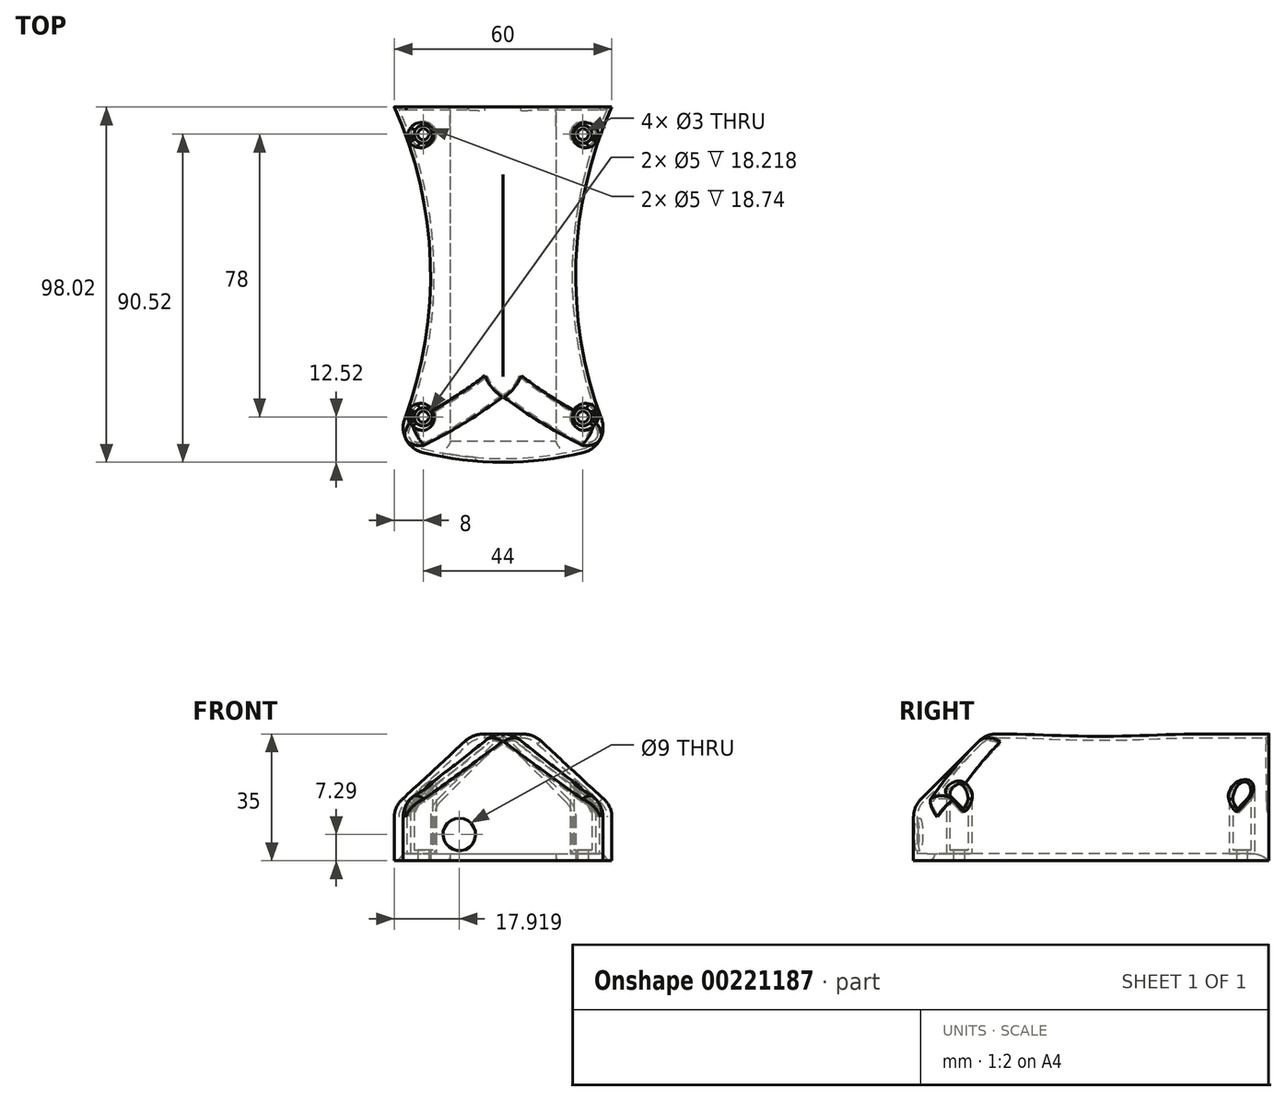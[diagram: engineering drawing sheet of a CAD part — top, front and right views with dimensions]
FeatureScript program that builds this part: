
annotation { "Feature Type Name" : "Feature", "Feature Type Description" : "" }
export const myFeature = defineFeature(function(context is Context, id is Id, definition is map)
    precondition{}
    {
        {
            var Q0;
            Q0=qCreatedBy(makeId("Top.planeOp"),FACE);
            var sketch = newSketch(context, id + "F0", { "sketchPlane" : qUnion([Q0])});
            skLineSegment(sketch, "E0.bottom", {"start": v(30, 46.5) * mm, "end": v(-30, 46.5) * mm});
            skPoint(sketch, "E0.middle", {"position": v(0, 0) * mm});
            skLineSegment(sketch, "E1.bottom", {"start": v(20.5, -39) * mm, "end": v(19.5, -39) * mm});
            skArc(sketch, "E2", {"start": v(30, 46.5) * mm, "mid": v(20.03, 2.3) * mm, "end": v(28.2, -42.26) * mm});
            skArc(sketch, "E3.MirrorCS", {"start": v(-30, 46.5) * mm, "mid": v(-20.03, 2.3) * mm, "end": v(-28.2, -42.26) * mm});
            skArc(sketch, "E4", {"start": v(-25.43, -47.94) * mm, "mid": v(0, -51.52) * mm, "end": v(25.43, -47.94) * mm});
            skCircle(sketch, "E5", {"center": v(-22, 39) * mm, "radius": 1.5 * mm});
            skCircle(sketch, "E6", {"center": v(22, 39) * mm, "radius": 1.5 * mm});
            skCircle(sketch, "E7", {"center": v(22, -39) * mm, "radius": 1.5 * mm});
            skCircle(sketch, "E8", {"center": v(-22, -39) * mm, "radius": 1.5 * mm});
            skLineSegment(sketch, "E9", {"start": v(28.2, -42.26) * mm, "end": v(25.43, -47.94) * mm});
            skLineSegment(sketch, "E10.MirrorCS", {"start": v(-28.2, -42.26) * mm, "end": v(-25.43, -47.94) * mm});
            skPoint(sketch, "E11.orphan", {"position": v(30, -46.5) * mm});
            skPoint(sketch, "E12.orphan", {"position": v(-30, -46.5) * mm});
            skCircle(sketch, "E13", {"center": v(-22, 39) * mm, "radius": 2.5 * mm});
            skCircle(sketch, "E14", {"center": v(22, 39) * mm, "radius": 2.5 * mm});
            skCircle(sketch, "E15", {"center": v(-22, -39) * mm, "radius": 2.5 * mm});
            skCircle(sketch, "E16", {"center": v(22, -39) * mm, "radius": 2.5 * mm});
            skLineSegment(sketch, "E17.bottom", {"start": v(16.76, 44.51) * mm, "end": v(-16.76, 44.51) * mm});
            skLineSegment(sketch, "E17.top", {"start": v(16.76, -44.51) * mm, "end": v(-16.76, -44.51) * mm});
            skLineSegment(sketch, "E17.left", {"start": v(16.76, 44.51) * mm, "end": v(16.76, -44.51) * mm});
            skLineSegment(sketch, "E17.right", {"start": v(-16.76, 44.51) * mm, "end": v(-16.76, -44.51) * mm});
            skSolve(sketch);
        }
        {
            var Q0;
            Q0=makeQuery(id+"F0.imprint","IMPRINT",FACE,{"disambiguationData":[TD([[makeQuery(id+"F0.imprint","IMPRINT",EDGE,{"derivedFrom":sQuery(id+"F0.wireOp",EDGE,"E0.bottom")}),1.0]])]});
            var Q1;
            Q1=makeQuery(id+"F0.imprint","IMPRINT",FACE,{"disambiguationData":[TD([[makeQuery(id+"F0.imprint","IMPRINT",EDGE,{"derivedFrom":sQuery(id+"F0.wireOp",EDGE,"E13")}),1.0]])]});
            var Q2;
            Q2=makeQuery(id+"F0.imprint","IMPRINT",FACE,{"disambiguationData":[TD([[makeQuery(id+"F0.imprint","IMPRINT",EDGE,{"derivedFrom":sQuery(id+"F0.wireOp",EDGE,"E14")}),1.0]])]});
            var Q3;
            Q3=makeQuery(id+"F0.imprint","IMPRINT",FACE,{"disambiguationData":[TD([[makeQuery(id+"F0.imprint","IMPRINT",EDGE,{"derivedFrom":sQuery(id+"F0.wireOp",EDGE,"E16")}),1.0]])]});
            var Q4;
            Q4=makeQuery(id+"F0.imprint","IMPRINT",FACE,{"disambiguationData":[TD([[makeQuery(id+"F0.imprint","IMPRINT",EDGE,{"derivedFrom":sQuery(id+"F0.wireOp",EDGE,"E15")}),1.0]])]});
            var Q5;
            Q5=makeQuery(id+"F0.imprint","IMPRINT",FACE,{"disambiguationData":[TD([[makeQuery(id+"F0.imprint","IMPRINT",EDGE,{"derivedFrom":sQuery(id+"F0.wireOp",EDGE,"SKrwtrik-Ue9O-fv6v-n90H-pNgHu3pozgwR")}),-1.0]])]});
            extrude(context, id + "F1", {"entities" : qUnion([Q0, Q1, Q2, Q3, Q4, Q5]), "depth" : 3 * mm});
        }
        {
            var Q0;
            Q0=makeQuery(id+"F0.imprint","IMPRINT",FACE,{"disambiguationData":[TD([[makeQuery(id+"F0.imprint","IMPRINT",EDGE,{"derivedFrom":sQuery(id+"F0.wireOp",EDGE,"E0.bottom")}),1.0]])]});
            var Q1;
            Q1=makeQuery(id+"F0.imprint","IMPRINT",FACE,{"disambiguationData":[TD([[makeQuery(id+"F0.imprint","IMPRINT",EDGE,{"derivedFrom":sQuery(id+"F0.wireOp",EDGE,"E17.bottom")}),1.0]])]});
            extrude(context, id + "F2", {"entities" : qUnion([Q0, Q1]), "operationType" : NewBodyOperationType.ADD, "depth" : 35 * mm});
        }
        {
            var Q0;
            Q0=makeQuery(id+"F2.opExtrude","CAP_EDGE",EDGE,{"disambiguationData":[OSD([sQuery(id+"F0.wireOp",EDGE,"E3.MirrorCS")])],"isStart":false});
            var Q1;
            Q1=makeQuery(id+"F2.opExtrude","CAP_EDGE",EDGE,{"disambiguationData":[OSD([sQuery(id+"F0.wireOp",EDGE,"E2")])],"isStart":false});
            var Q2;
            Q2=makeQuery(id+"F2.opExtrude","CAP_EDGE",EDGE,{"disambiguationData":[OSD([sQuery(id+"F0.wireOp",EDGE,"E4")])],"isStart":false});
            chamfer(context, id + "F3", {"entities" : qUnion([Q0, Q1, Q2]), "width" : 20 * mm, "tangentPropagation" : true});
        }
        {
            var Q0;
            {var subQ0=sQuery(id+"F0.wireOp",EDGE,"E3.MirrorCS");Q0=makeQuery(id+"F3.opChamfer","BLEND_EDGE",EDGE,{"blendedFrom":[makeQuery(id+"F2.opExtrude","CAP_EDGE",EDGE,{"disambiguationData":[OSD([subQ0])],"isStart":false}),makeQuery(id+"F2.boolean.opBoolean","MERGE",FACE,{"derivedFrom":[makeQuery(id+"F1.opExtrude","SWEPT_FACE",FACE,{"disambiguationData":[OSD([subQ0])]}),makeQuery(id+"F2.opExtrude","SWEPT_FACE",FACE,{"disambiguationData":[OSD([subQ0])]})]})],"blendedInto":[makeQuery(id+"F2.boolean.opBoolean","MERGE",FACE,{"derivedFrom":[makeQuery(id+"F1.opExtrude","SWEPT_FACE",FACE,{"disambiguationData":[OSD([subQ0])]}),makeQuery(id+"F2.opExtrude","SWEPT_FACE",FACE,{"disambiguationData":[OSD([subQ0])]})]})]});}
            var Q1;
            {var subQ0=sQuery(id+"F0.wireOp",EDGE,"E2");Q1=makeQuery(id+"F3.opChamfer","BLEND_EDGE",EDGE,{"blendedFrom":[makeQuery(id+"F2.opExtrude","CAP_EDGE",EDGE,{"disambiguationData":[OSD([subQ0])],"isStart":false}),makeQuery(id+"F2.opExtrude","CAP_FACE",FACE,{"disambiguationData":[OSD([sQuery(id+"F0.wireOp",EDGE,"E0.bottom"),subQ0,sQuery(id+"F0.wireOp",EDGE,"E3.MirrorCS"),sQuery(id+"F0.wireOp",EDGE,"E4"),sQuery(id+"F0.wireOp",EDGE,"E9"),sQuery(id+"F0.wireOp",EDGE,"E10.MirrorCS"),sQuery(id+"F0.wireOp",EDGE,"SKrwtrik-Ue9O-fv6v-n90H-pNgHu3pozgwR"),sQuery(id+"F0.wireOp",EDGE,"E13"),sQuery(id+"F0.wireOp",EDGE,"E14"),sQuery(id+"F0.wireOp",EDGE,"E15"),sQuery(id+"F0.wireOp",EDGE,"E16")])],"isStart":false})],"blendedInto":[makeQuery(id+"F2.opExtrude","CAP_FACE",FACE,{"disambiguationData":[OSD([sQuery(id+"F0.wireOp",EDGE,"E0.bottom"),subQ0,sQuery(id+"F0.wireOp",EDGE,"E3.MirrorCS"),sQuery(id+"F0.wireOp",EDGE,"E4"),sQuery(id+"F0.wireOp",EDGE,"E9"),sQuery(id+"F0.wireOp",EDGE,"E10.MirrorCS"),sQuery(id+"F0.wireOp",EDGE,"SKrwtrik-Ue9O-fv6v-n90H-pNgHu3pozgwR"),sQuery(id+"F0.wireOp",EDGE,"E13"),sQuery(id+"F0.wireOp",EDGE,"E14"),sQuery(id+"F0.wireOp",EDGE,"E15"),sQuery(id+"F0.wireOp",EDGE,"E16")])],"isStart":false})]});}
            var Q2;
            {var subQ0=sQuery(id+"F0.wireOp",EDGE,"E3.MirrorCS");Q2=makeQuery(id+"F3.opChamfer","BLEND_EDGE",EDGE,{"blendedFrom":[makeQuery(id+"F2.opExtrude","CAP_EDGE",EDGE,{"disambiguationData":[OSD([subQ0])],"isStart":false}),makeQuery(id+"F2.opExtrude","CAP_FACE",FACE,{"disambiguationData":[OSD([sQuery(id+"F0.wireOp",EDGE,"E0.bottom"),sQuery(id+"F0.wireOp",EDGE,"E2"),subQ0,sQuery(id+"F0.wireOp",EDGE,"E4"),sQuery(id+"F0.wireOp",EDGE,"E9"),sQuery(id+"F0.wireOp",EDGE,"E10.MirrorCS"),sQuery(id+"F0.wireOp",EDGE,"SKrwtrik-Ue9O-fv6v-n90H-pNgHu3pozgwR"),sQuery(id+"F0.wireOp",EDGE,"E13"),sQuery(id+"F0.wireOp",EDGE,"E14"),sQuery(id+"F0.wireOp",EDGE,"E15"),sQuery(id+"F0.wireOp",EDGE,"E16")])],"isStart":false})],"blendedInto":[makeQuery(id+"F2.opExtrude","CAP_FACE",FACE,{"disambiguationData":[OSD([sQuery(id+"F0.wireOp",EDGE,"E0.bottom"),sQuery(id+"F0.wireOp",EDGE,"E2"),subQ0,sQuery(id+"F0.wireOp",EDGE,"E4"),sQuery(id+"F0.wireOp",EDGE,"E9"),sQuery(id+"F0.wireOp",EDGE,"E10.MirrorCS"),sQuery(id+"F0.wireOp",EDGE,"SKrwtrik-Ue9O-fv6v-n90H-pNgHu3pozgwR"),sQuery(id+"F0.wireOp",EDGE,"E13"),sQuery(id+"F0.wireOp",EDGE,"E14"),sQuery(id+"F0.wireOp",EDGE,"E15"),sQuery(id+"F0.wireOp",EDGE,"E16")])],"isStart":false})]});}
            var Q3;
            {var subQ0=sQuery(id+"F0.wireOp",EDGE,"E2");Q3=makeQuery(id+"F3.opChamfer","BLEND_EDGE",EDGE,{"blendedFrom":[makeQuery(id+"F2.opExtrude","CAP_EDGE",EDGE,{"disambiguationData":[OSD([subQ0])],"isStart":false}),makeQuery(id+"F2.boolean.opBoolean","MERGE",FACE,{"derivedFrom":[makeQuery(id+"F1.opExtrude","SWEPT_FACE",FACE,{"disambiguationData":[OSD([subQ0])]}),makeQuery(id+"F2.opExtrude","SWEPT_FACE",FACE,{"disambiguationData":[OSD([subQ0])]})]})],"blendedInto":[makeQuery(id+"F2.boolean.opBoolean","MERGE",FACE,{"derivedFrom":[makeQuery(id+"F1.opExtrude","SWEPT_FACE",FACE,{"disambiguationData":[OSD([subQ0])]}),makeQuery(id+"F2.opExtrude","SWEPT_FACE",FACE,{"disambiguationData":[OSD([subQ0])]})]})]});}
            var Q4;
            Q4=makeQuery(id+"F3.opChamfer","BLEND_EDGE",EDGE,{"blendedFrom":[makeQuery(id+"F2.opExtrude","CAP_EDGE",EDGE,{"disambiguationData":[OSD([sQuery(id+"F0.wireOp",EDGE,"E2")])],"isStart":false}),makeQuery(id+"F2.opExtrude","CAP_EDGE",EDGE,{"disambiguationData":[OSD([sQuery(id+"F0.wireOp",EDGE,"E4")])],"isStart":false})],"blendedInto":[]});
            var Q5;
            Q5=makeQuery(id+"F3.opChamfer","BLEND_EDGE",EDGE,{"blendedFrom":[makeQuery(id+"F2.opExtrude","CAP_EDGE",EDGE,{"disambiguationData":[OSD([sQuery(id+"F0.wireOp",EDGE,"E3.MirrorCS")])],"isStart":false}),makeQuery(id+"F2.opExtrude","CAP_EDGE",EDGE,{"disambiguationData":[OSD([sQuery(id+"F0.wireOp",EDGE,"E4")])],"isStart":false})],"blendedInto":[]});
            var Q6;
            {var subQ0=sQuery(id+"F0.wireOp",EDGE,"E4");Q6=makeQuery(id+"F3.opChamfer","BLEND_EDGE",EDGE,{"blendedFrom":[makeQuery(id+"F2.opExtrude","CAP_EDGE",EDGE,{"disambiguationData":[OSD([subQ0])],"isStart":false}),makeQuery(id+"F2.opExtrude","CAP_FACE",FACE,{"disambiguationData":[OSD([sQuery(id+"F0.wireOp",EDGE,"E0.bottom"),sQuery(id+"F0.wireOp",EDGE,"E2"),sQuery(id+"F0.wireOp",EDGE,"E3.MirrorCS"),subQ0,sQuery(id+"F0.wireOp",EDGE,"E9"),sQuery(id+"F0.wireOp",EDGE,"E10.MirrorCS"),sQuery(id+"F0.wireOp",EDGE,"SKrwtrik-Ue9O-fv6v-n90H-pNgHu3pozgwR"),sQuery(id+"F0.wireOp",EDGE,"E13"),sQuery(id+"F0.wireOp",EDGE,"E14"),sQuery(id+"F0.wireOp",EDGE,"E15"),sQuery(id+"F0.wireOp",EDGE,"E16")])],"isStart":false})],"blendedInto":[makeQuery(id+"F2.opExtrude","CAP_FACE",FACE,{"disambiguationData":[OSD([sQuery(id+"F0.wireOp",EDGE,"E0.bottom"),sQuery(id+"F0.wireOp",EDGE,"E2"),sQuery(id+"F0.wireOp",EDGE,"E3.MirrorCS"),subQ0,sQuery(id+"F0.wireOp",EDGE,"E9"),sQuery(id+"F0.wireOp",EDGE,"E10.MirrorCS"),sQuery(id+"F0.wireOp",EDGE,"SKrwtrik-Ue9O-fv6v-n90H-pNgHu3pozgwR"),sQuery(id+"F0.wireOp",EDGE,"E13"),sQuery(id+"F0.wireOp",EDGE,"E14"),sQuery(id+"F0.wireOp",EDGE,"E15"),sQuery(id+"F0.wireOp",EDGE,"E16")])],"isStart":false})]});}
            var Q7;
            {var subQ0=sQuery(id+"F0.wireOp",EDGE,"E4");Q7=makeQuery(id+"F3.opChamfer","BLEND_EDGE",EDGE,{"blendedFrom":[makeQuery(id+"F2.opExtrude","CAP_EDGE",EDGE,{"disambiguationData":[OSD([subQ0])],"isStart":false}),makeQuery(id+"F2.boolean.opBoolean","MERGE",FACE,{"derivedFrom":[makeQuery(id+"F1.opExtrude","SWEPT_FACE",FACE,{"disambiguationData":[OSD([subQ0])]}),makeQuery(id+"F2.opExtrude","SWEPT_FACE",FACE,{"disambiguationData":[OSD([subQ0])]})]})],"blendedInto":[makeQuery(id+"F2.boolean.opBoolean","MERGE",FACE,{"derivedFrom":[makeQuery(id+"F1.opExtrude","SWEPT_FACE",FACE,{"disambiguationData":[OSD([subQ0])]}),makeQuery(id+"F2.opExtrude","SWEPT_FACE",FACE,{"disambiguationData":[OSD([subQ0])]})]})]});}
            var Q8;
            {var subQ0=sQuery(id+"F0.wireOp",EDGE,"E9");Q8=makeQuery(id+"F3.opChamfer","BLEND_EDGE",EDGE,{"blendedFrom":[makeQuery(id+"F2.opExtrude","CAP_EDGE",EDGE,{"disambiguationData":[OSD([sQuery(id+"F0.wireOp",EDGE,"E2")])],"isStart":false}),makeQuery(id+"F2.boolean.opBoolean","MERGE",FACE,{"derivedFrom":[makeQuery(id+"F1.opExtrude","SWEPT_FACE",FACE,{"disambiguationData":[OSD([subQ0])]}),makeQuery(id+"F2.opExtrude","SWEPT_FACE",FACE,{"disambiguationData":[OSD([subQ0])]})]})],"blendedInto":[makeQuery(id+"F2.boolean.opBoolean","MERGE",FACE,{"derivedFrom":[makeQuery(id+"F1.opExtrude","SWEPT_FACE",FACE,{"disambiguationData":[OSD([subQ0])]}),makeQuery(id+"F2.opExtrude","SWEPT_FACE",FACE,{"disambiguationData":[OSD([subQ0])]})]})]});}
            var Q9;
            {var subQ0=sQuery(id+"F0.wireOp",EDGE,"E9");Q9=makeQuery(id+"F3.opChamfer","BLEND_EDGE",EDGE,{"blendedFrom":[makeQuery(id+"F2.opExtrude","CAP_EDGE",EDGE,{"disambiguationData":[OSD([sQuery(id+"F0.wireOp",EDGE,"E4")])],"isStart":false}),makeQuery(id+"F2.boolean.opBoolean","MERGE",FACE,{"derivedFrom":[makeQuery(id+"F1.opExtrude","SWEPT_FACE",FACE,{"disambiguationData":[OSD([subQ0])]}),makeQuery(id+"F2.opExtrude","SWEPT_FACE",FACE,{"disambiguationData":[OSD([subQ0])]})]})],"blendedInto":[makeQuery(id+"F2.boolean.opBoolean","MERGE",FACE,{"derivedFrom":[makeQuery(id+"F1.opExtrude","SWEPT_FACE",FACE,{"disambiguationData":[OSD([subQ0])]}),makeQuery(id+"F2.opExtrude","SWEPT_FACE",FACE,{"disambiguationData":[OSD([subQ0])]})]})]});}
            var Q10;
            {var subQ0=sQuery(id+"F0.wireOp",EDGE,"E9");var subQ1=sQuery(id+"F0.wireOp",EDGE,"E4");Q10=makeQuery(id+"F2.boolean.opBoolean","MERGE",EDGE,{"derivedFrom":[makeQuery(id+"F1.opExtrude","SWEPT_EDGE",EDGE,{"disambiguationData":[OSD([subQ1,subQ0])]}),makeQuery(id+"F2.opExtrude","SWEPT_EDGE",EDGE,{"disambiguationData":[OSD([subQ1,subQ0])]})]});}
            var Q11;
            {var subQ0=sQuery(id+"F0.wireOp",EDGE,"E9");var subQ1=sQuery(id+"F0.wireOp",EDGE,"E2");Q11=makeQuery(id+"F2.boolean.opBoolean","MERGE",EDGE,{"derivedFrom":[makeQuery(id+"F1.opExtrude","SWEPT_EDGE",EDGE,{"disambiguationData":[OSD([subQ1,subQ0])]}),makeQuery(id+"F2.opExtrude","SWEPT_EDGE",EDGE,{"disambiguationData":[OSD([subQ1,subQ0])]})]});}
            var Q12;
            {var subQ0=sQuery(id+"F0.wireOp",EDGE,"E10.MirrorCS");Q12=makeQuery(id+"F3.opChamfer","BLEND_EDGE",EDGE,{"blendedFrom":[makeQuery(id+"F2.opExtrude","CAP_EDGE",EDGE,{"disambiguationData":[OSD([sQuery(id+"F0.wireOp",EDGE,"E4")])],"isStart":false}),makeQuery(id+"F2.boolean.opBoolean","MERGE",FACE,{"derivedFrom":[makeQuery(id+"F1.opExtrude","SWEPT_FACE",FACE,{"disambiguationData":[OSD([subQ0])]}),makeQuery(id+"F2.opExtrude","SWEPT_FACE",FACE,{"disambiguationData":[OSD([subQ0])]})]})],"blendedInto":[makeQuery(id+"F2.boolean.opBoolean","MERGE",FACE,{"derivedFrom":[makeQuery(id+"F1.opExtrude","SWEPT_FACE",FACE,{"disambiguationData":[OSD([subQ0])]}),makeQuery(id+"F2.opExtrude","SWEPT_FACE",FACE,{"disambiguationData":[OSD([subQ0])]})]})]});}
            var Q13;
            {var subQ0=sQuery(id+"F0.wireOp",EDGE,"E10.MirrorCS");Q13=makeQuery(id+"F3.opChamfer","BLEND_EDGE",EDGE,{"blendedFrom":[makeQuery(id+"F2.opExtrude","CAP_EDGE",EDGE,{"disambiguationData":[OSD([sQuery(id+"F0.wireOp",EDGE,"E3.MirrorCS")])],"isStart":false}),makeQuery(id+"F2.boolean.opBoolean","MERGE",FACE,{"derivedFrom":[makeQuery(id+"F1.opExtrude","SWEPT_FACE",FACE,{"disambiguationData":[OSD([subQ0])]}),makeQuery(id+"F2.opExtrude","SWEPT_FACE",FACE,{"disambiguationData":[OSD([subQ0])]})]})],"blendedInto":[makeQuery(id+"F2.boolean.opBoolean","MERGE",FACE,{"derivedFrom":[makeQuery(id+"F1.opExtrude","SWEPT_FACE",FACE,{"disambiguationData":[OSD([subQ0])]}),makeQuery(id+"F2.opExtrude","SWEPT_FACE",FACE,{"disambiguationData":[OSD([subQ0])]})]})]});}
            var Q14;
            {var subQ0=sQuery(id+"F0.wireOp",EDGE,"E10.MirrorCS");var subQ1=sQuery(id+"F0.wireOp",EDGE,"E3.MirrorCS");Q14=makeQuery(id+"F2.boolean.opBoolean","MERGE",EDGE,{"derivedFrom":[makeQuery(id+"F1.opExtrude","SWEPT_EDGE",EDGE,{"disambiguationData":[OSD([subQ1,subQ0])]}),makeQuery(id+"F2.opExtrude","SWEPT_EDGE",EDGE,{"disambiguationData":[OSD([subQ1,subQ0])]})]});}
            var Q15;
            {var subQ0=sQuery(id+"F0.wireOp",EDGE,"E10.MirrorCS");var subQ1=sQuery(id+"F0.wireOp",EDGE,"E4");Q15=makeQuery(id+"F2.boolean.opBoolean","MERGE",EDGE,{"derivedFrom":[makeQuery(id+"F1.opExtrude","SWEPT_EDGE",EDGE,{"disambiguationData":[OSD([subQ1,subQ0])]}),makeQuery(id+"F2.opExtrude","SWEPT_EDGE",EDGE,{"disambiguationData":[OSD([subQ1,subQ0])]})]});}
            fillet(context, id + "F4", {"entities" : qUnion([Q0, Q1, Q2, Q3, Q4, Q5, Q6, Q7, Q8, Q9, Q10, Q11, Q12, Q13, Q14, Q15]), "radius" : 7 * mm, "tangentPropagation" : true, "allowEdgeOverflow" : false});
        }
        {
            var Q0;
            Q0=makeQuery(id+"F3.opChamfer","BLEND_EDGE",EDGE,{"blendedFrom":[makeQuery(id+"F2.opExtrude","CAP_EDGE",EDGE,{"disambiguationData":[OSD([sQuery(id+"F0.wireOp",EDGE,"E2")])],"isStart":false}),makeQuery(id+"F2.opExtrude","SWEPT_FACE",FACE,{"disambiguationData":[OSD([sQuery(id+"F0.wireOp",EDGE,"E14")])]})],"blendedInto":[makeQuery(id+"F2.opExtrude","SWEPT_FACE",FACE,{"disambiguationData":[OSD([sQuery(id+"F0.wireOp",EDGE,"E14")])]})]});
            var Q1;
            Q1=makeQuery(id+"F3.opChamfer","BLEND_EDGE",EDGE,{"blendedFrom":[makeQuery(id+"F2.opExtrude","CAP_EDGE",EDGE,{"disambiguationData":[OSD([sQuery(id+"F0.wireOp",EDGE,"E3.MirrorCS")])],"isStart":false}),makeQuery(id+"F2.opExtrude","SWEPT_FACE",FACE,{"disambiguationData":[OSD([sQuery(id+"F0.wireOp",EDGE,"E13")])]})],"blendedInto":[makeQuery(id+"F2.opExtrude","SWEPT_FACE",FACE,{"disambiguationData":[OSD([sQuery(id+"F0.wireOp",EDGE,"E13")])]})]});
            var Q2;
            Q2=makeQuery(id+"F3.opChamfer","BLEND_EDGE",EDGE,{"blendedFrom":[makeQuery(id+"F2.opExtrude","CAP_EDGE",EDGE,{"disambiguationData":[OSD([sQuery(id+"F0.wireOp",EDGE,"E3.MirrorCS")])],"isStart":false}),makeQuery(id+"F2.opExtrude","SWEPT_FACE",FACE,{"disambiguationData":[OSD([sQuery(id+"F0.wireOp",EDGE,"E15")])]})],"blendedInto":[makeQuery(id+"F2.opExtrude","SWEPT_FACE",FACE,{"disambiguationData":[OSD([sQuery(id+"F0.wireOp",EDGE,"E15")])]})]});
            var Q3;
            Q3=makeQuery(id+"F4.opFillet","BLEND_EDGE",EDGE,{"blendedFrom":[makeQuery(id+"F3.opChamfer","BLEND_EDGE",EDGE,{"blendedFrom":[makeQuery(id+"F2.opExtrude","CAP_EDGE",EDGE,{"disambiguationData":[OSD([sQuery(id+"F0.wireOp",EDGE,"E3.MirrorCS")])],"isStart":false}),makeQuery(id+"F2.opExtrude","CAP_EDGE",EDGE,{"disambiguationData":[OSD([sQuery(id+"F0.wireOp",EDGE,"E4")])],"isStart":false})],"blendedInto":[]}),makeQuery(id+"F2.opExtrude","SWEPT_FACE",FACE,{"disambiguationData":[OSD([sQuery(id+"F0.wireOp",EDGE,"E15")])]})],"blendedInto":[makeQuery(id+"F2.opExtrude","SWEPT_FACE",FACE,{"disambiguationData":[OSD([sQuery(id+"F0.wireOp",EDGE,"E15")])]})]});
            var Q4;
            Q4=makeQuery(id+"F3.opChamfer","BLEND_EDGE",EDGE,{"blendedFrom":[makeQuery(id+"F2.opExtrude","CAP_EDGE",EDGE,{"disambiguationData":[OSD([sQuery(id+"F0.wireOp",EDGE,"E2")])],"isStart":false}),makeQuery(id+"F2.opExtrude","SWEPT_FACE",FACE,{"disambiguationData":[OSD([sQuery(id+"F0.wireOp",EDGE,"E16")])]})],"blendedInto":[makeQuery(id+"F2.opExtrude","SWEPT_FACE",FACE,{"disambiguationData":[OSD([sQuery(id+"F0.wireOp",EDGE,"E16")])]})]});
            var Q5;
            Q5=makeQuery(id+"F4.opFillet","BLEND_EDGE",EDGE,{"blendedFrom":[makeQuery(id+"F3.opChamfer","BLEND_EDGE",EDGE,{"blendedFrom":[makeQuery(id+"F2.opExtrude","CAP_EDGE",EDGE,{"disambiguationData":[OSD([sQuery(id+"F0.wireOp",EDGE,"E2")])],"isStart":false}),makeQuery(id+"F2.opExtrude","CAP_EDGE",EDGE,{"disambiguationData":[OSD([sQuery(id+"F0.wireOp",EDGE,"E4")])],"isStart":false})],"blendedInto":[]}),makeQuery(id+"F2.opExtrude","SWEPT_FACE",FACE,{"disambiguationData":[OSD([sQuery(id+"F0.wireOp",EDGE,"E16")])]})],"blendedInto":[makeQuery(id+"F2.opExtrude","SWEPT_FACE",FACE,{"disambiguationData":[OSD([sQuery(id+"F0.wireOp",EDGE,"E16")])]})]});
            fillet(context, id + "F5", {"entities" : qUnion([Q0, Q1, Q2, Q3, Q4, Q5]), "radius" : 1 * mm, "tangentPropagation" : true, "allowEdgeOverflow" : false});
        }
        {
            var Q0;
            {var subQ0=sQuery(id+"F0.wireOp",EDGE,"E0.bottom");Q0=makeQuery(id+"F2.boolean.opBoolean","MERGE",FACE,{"derivedFrom":[makeQuery(id+"F1.opExtrude","SWEPT_FACE",FACE,{"disambiguationData":[OSD([subQ0])]}),makeQuery(id+"F2.opExtrude","SWEPT_FACE",FACE,{"disambiguationData":[OSD([subQ0])]})]});}
            shell(context, id + "F6", {"entities" : qUnion([Q0]), "thickness" : 1 * mm});
        }
        {
            var Q0;
            Q0=makeQuery(id+"F6.opShell","OFFSET_FACE",FACE,{"disambiguationData":[OSD([sQuery(id+"F0.wireOp",EDGE,"E0.bottom"),sQuery(id+"F0.wireOp",EDGE,"E2"),sQuery(id+"F0.wireOp",EDGE,"E3.MirrorCS"),sQuery(id+"F0.wireOp",EDGE,"E4"),sQuery(id+"F0.wireOp",EDGE,"E5"),sQuery(id+"F0.wireOp",EDGE,"E6"),sQuery(id+"F0.wireOp",EDGE,"E7"),sQuery(id+"F0.wireOp",EDGE,"E8"),sQuery(id+"F0.wireOp",EDGE,"E9"),sQuery(id+"F0.wireOp",EDGE,"E10.MirrorCS"),sQuery(id+"F0.wireOp",EDGE,"E13"),sQuery(id+"F0.wireOp",EDGE,"E14"),sQuery(id+"F0.wireOp",EDGE,"E15"),sQuery(id+"F0.wireOp",EDGE,"E16"),sQuery(id+"F0.wireOp",EDGE,"E17.bottom"),sQuery(id+"F0.wireOp",EDGE,"E17.top"),sQuery(id+"F0.wireOp",EDGE,"E17.left"),sQuery(id+"F0.wireOp",EDGE,"E17.right")])]});
            extrude(context, id + "F7", {"entities" : qUnion([Q0]), "operationType" : NewBodyOperationType.ADD, "depth" : 1 * mm});
        }
        {
            var Q0;
            Q0=makeQuery(id+"F7.opExtrude","CAP_FACE",FACE,{"disambiguationData":[OSD([sQuery(id+"F0.wireOp",EDGE,"E0.bottom"),sQuery(id+"F0.wireOp",EDGE,"E2"),sQuery(id+"F0.wireOp",EDGE,"E3.MirrorCS"),sQuery(id+"F0.wireOp",EDGE,"E4"),sQuery(id+"F0.wireOp",EDGE,"E5"),sQuery(id+"F0.wireOp",EDGE,"E6"),sQuery(id+"F0.wireOp",EDGE,"E7"),sQuery(id+"F0.wireOp",EDGE,"E8"),sQuery(id+"F0.wireOp",EDGE,"E9"),sQuery(id+"F0.wireOp",EDGE,"E10.MirrorCS"),sQuery(id+"F0.wireOp",EDGE,"E13"),sQuery(id+"F0.wireOp",EDGE,"E14"),sQuery(id+"F0.wireOp",EDGE,"E15"),sQuery(id+"F0.wireOp",EDGE,"E16"),sQuery(id+"F0.wireOp",EDGE,"E17.bottom"),sQuery(id+"F0.wireOp",EDGE,"E17.top"),sQuery(id+"F0.wireOp",EDGE,"E17.left"),sQuery(id+"F0.wireOp",EDGE,"E17.right")])],"isStart":false});
            var sketch = newSketch(context, id + "F8", { "sketchPlane" : qUnion([Q0])});
            skLineSegment(sketch, "E18.bottom", {"start": v(-14.58, 54.73) * mm, "end": v(14.58, 54.73) * mm});
            skLineSegment(sketch, "E18.top", {"start": v(-14.58, -45.6) * mm, "end": v(14.58, -45.6) * mm});
            skLineSegment(sketch, "E18.left", {"start": v(-14.58, 54.73) * mm, "end": v(-14.58, -45.6) * mm});
            skLineSegment(sketch, "E18.right", {"start": v(14.58, 54.73) * mm, "end": v(14.58, -45.6) * mm});
            skPoint(sketch, "E18.middle", {"position": v(0, 4.56) * mm});
            skSolve(sketch);
        }
        {
            var Q0;
            {var subQ0=sQuery(id+"F8.wireOp",EDGE,"E18.top");Q0=makeQuery(id+"F8.imprint","IMPRINT",FACE,{"disambiguationData":[TD([[makeQuery(id+"F8.imprint","IMPRINT",EDGE,{"derivedFrom":subQ0}),1.0]])]});}
            extrude(context, id + "F9", {"entities" : qUnion([Q0]), "operationType" : NewBodyOperationType.REMOVE, "oppositeDirection" : true, "depth" : 3 * mm});
        }
        {
            var Q0;
            Q0=makeQuery(id+"F9.boolean.opBoolean","COPY",EDGE,{"derivedFrom":makeQuery(id+"F9.opExtrude","CAP_EDGE",EDGE,{"disambiguationData":[OSD([sQuery(id+"F8.wireOp",EDGE,"E18.right")])],"isStart":true})});
            var Q1;
            {var subQ0=sQuery(id+"F0.wireOp",EDGE,"E10.MirrorCS");var subQ1=sQuery(id+"F0.wireOp",EDGE,"E9");var subQ2=sQuery(id+"F0.wireOp",EDGE,"E4");var subQ3=sQuery(id+"F0.wireOp",EDGE,"E3.MirrorCS");var subQ4=sQuery(id+"F0.wireOp",EDGE,"E2");var subQ5=sQuery(id+"F0.wireOp",EDGE,"E0.bottom");Q1=makeQuery(id+"F9.boolean.opBoolean","INTERSECT",EDGE,{"derivedFrom":[makeQuery(id+"F2.boolean.opBoolean","MERGE",FACE,{"derivedFrom":[makeQuery(id+"F1.opExtrude","CAP_FACE",FACE,{"disambiguationData":[OSD([subQ5,subQ4,subQ3,subQ2,sQuery(id+"F0.wireOp",EDGE,"E5"),sQuery(id+"F0.wireOp",EDGE,"E6"),sQuery(id+"F0.wireOp",EDGE,"E7"),sQuery(id+"F0.wireOp",EDGE,"E8"),subQ1,subQ0,sQuery(id+"F0.wireOp",EDGE,"E17.bottom"),sQuery(id+"F0.wireOp",EDGE,"E17.top"),sQuery(id+"F0.wireOp",EDGE,"E17.left"),sQuery(id+"F0.wireOp",EDGE,"E17.right")])],"isStart":true}),makeQuery(id+"F2.opExtrude","CAP_FACE",FACE,{"disambiguationData":[OSD([subQ5,subQ4,subQ3,subQ2,subQ1,subQ0,sQuery(id+"F0.wireOp",EDGE,"E13"),sQuery(id+"F0.wireOp",EDGE,"E14"),sQuery(id+"F0.wireOp",EDGE,"E15"),sQuery(id+"F0.wireOp",EDGE,"E16")])],"isStart":true})]}),makeQuery(id+"F9.opExtrude","SWEPT_FACE",FACE,{"disambiguationData":[OSD([sQuery(id+"F8.wireOp",EDGE,"E18.right")])]})]});}
            var Q2;
            Q2=makeQuery(id+"F9.boolean.opBoolean","COPY",EDGE,{"derivedFrom":makeQuery(id+"F9.opExtrude","CAP_EDGE",EDGE,{"disambiguationData":[OSD([sQuery(id+"F8.wireOp",EDGE,"E18.left")])],"isStart":true})});
            var Q3;
            {var subQ0=sQuery(id+"F0.wireOp",EDGE,"E10.MirrorCS");var subQ1=sQuery(id+"F0.wireOp",EDGE,"E9");var subQ2=sQuery(id+"F0.wireOp",EDGE,"E4");var subQ3=sQuery(id+"F0.wireOp",EDGE,"E3.MirrorCS");var subQ4=sQuery(id+"F0.wireOp",EDGE,"E2");var subQ5=sQuery(id+"F0.wireOp",EDGE,"E0.bottom");Q3=makeQuery(id+"F9.boolean.opBoolean","INTERSECT",EDGE,{"derivedFrom":[makeQuery(id+"F2.boolean.opBoolean","MERGE",FACE,{"derivedFrom":[makeQuery(id+"F1.opExtrude","CAP_FACE",FACE,{"disambiguationData":[OSD([subQ5,subQ4,subQ3,subQ2,sQuery(id+"F0.wireOp",EDGE,"E5"),sQuery(id+"F0.wireOp",EDGE,"E6"),sQuery(id+"F0.wireOp",EDGE,"E7"),sQuery(id+"F0.wireOp",EDGE,"E8"),subQ1,subQ0,sQuery(id+"F0.wireOp",EDGE,"E17.bottom"),sQuery(id+"F0.wireOp",EDGE,"E17.top"),sQuery(id+"F0.wireOp",EDGE,"E17.left"),sQuery(id+"F0.wireOp",EDGE,"E17.right")])],"isStart":true}),makeQuery(id+"F2.opExtrude","CAP_FACE",FACE,{"disambiguationData":[OSD([subQ5,subQ4,subQ3,subQ2,subQ1,subQ0,sQuery(id+"F0.wireOp",EDGE,"E13"),sQuery(id+"F0.wireOp",EDGE,"E14"),sQuery(id+"F0.wireOp",EDGE,"E15"),sQuery(id+"F0.wireOp",EDGE,"E16")])],"isStart":true})]}),makeQuery(id+"F9.opExtrude","SWEPT_FACE",FACE,{"disambiguationData":[OSD([sQuery(id+"F8.wireOp",EDGE,"E18.left")])]})]});}
            fillet(context, id + "F10", {"entities" : qUnion([Q0, Q1, Q2, Q3]), "radius" : 1 * mm, "tangentPropagation" : true, "allowEdgeOverflow" : false});
        }
        {
            var Q0;
            {var subQ0=sQuery(id+"F0.wireOp",EDGE,"E3.MirrorCS");var subQ1=sQuery(id+"F0.wireOp",EDGE,"E0.bottom");Q0=makeQuery(id+"F6.opShell","OFFSET_EDGE",EDGE,{"disambiguationData":[OSD([subQ1,subQ0]),TDD([makeQuery(id+"F2.boolean.opBoolean","MERGE",EDGE,{"derivedFrom":[makeQuery(id+"F1.opExtrude","SWEPT_EDGE",EDGE,{"disambiguationData":[OSD([subQ1,subQ0])]}),makeQuery(id+"F2.opExtrude","SWEPT_EDGE",EDGE,{"disambiguationData":[OSD([subQ1,subQ0])]})]})])]});}
            var Q1;
            {var subQ0=sQuery(id+"F0.wireOp",EDGE,"E0.bottom");var subQ1=sQuery(id+"F0.wireOp",EDGE,"E3.MirrorCS");Q1=makeQuery(id+"F6.opShell","OFFSET_EDGE",EDGE,{"disambiguationData":[OSD([subQ0,subQ1]),TDD([makeQuery(id+"F4.opFillet","BLEND_EDGE",EDGE,{"blendedFrom":[makeQuery(id+"F3.opChamfer","BLEND_EDGE",EDGE,{"blendedFrom":[makeQuery(id+"F2.opExtrude","CAP_EDGE",EDGE,{"disambiguationData":[OSD([subQ1])],"isStart":false}),makeQuery(id+"F2.boolean.opBoolean","MERGE",FACE,{"derivedFrom":[makeQuery(id+"F1.opExtrude","SWEPT_FACE",FACE,{"disambiguationData":[OSD([subQ1])]}),makeQuery(id+"F2.opExtrude","SWEPT_FACE",FACE,{"disambiguationData":[OSD([subQ1])]})]})],"blendedInto":[makeQuery(id+"F2.boolean.opBoolean","MERGE",FACE,{"derivedFrom":[makeQuery(id+"F1.opExtrude","SWEPT_FACE",FACE,{"disambiguationData":[OSD([subQ1])]}),makeQuery(id+"F2.opExtrude","SWEPT_FACE",FACE,{"disambiguationData":[OSD([subQ1])]})]})]}),makeQuery(id+"F2.boolean.opBoolean","MERGE",FACE,{"derivedFrom":[makeQuery(id+"F1.opExtrude","SWEPT_FACE",FACE,{"disambiguationData":[OSD([subQ0])]}),makeQuery(id+"F2.opExtrude","SWEPT_FACE",FACE,{"disambiguationData":[OSD([subQ0])]})]})],"blendedInto":[makeQuery(id+"F2.boolean.opBoolean","MERGE",FACE,{"derivedFrom":[makeQuery(id+"F1.opExtrude","SWEPT_FACE",FACE,{"disambiguationData":[OSD([subQ0])]}),makeQuery(id+"F2.opExtrude","SWEPT_FACE",FACE,{"disambiguationData":[OSD([subQ0])]})]})]})])]});}
            var Q2;
            {var subQ0=sQuery(id+"F0.wireOp",EDGE,"E0.bottom");var subQ1=sQuery(id+"F0.wireOp",EDGE,"E3.MirrorCS");Q2=makeQuery(id+"F6.opShell","OFFSET_EDGE",EDGE,{"disambiguationData":[OSD([subQ0,subQ1]),TDD([makeQuery(id+"F3.opChamfer","BLEND_EDGE",EDGE,{"blendedFrom":[makeQuery(id+"F2.opExtrude","CAP_EDGE",EDGE,{"disambiguationData":[OSD([subQ1])],"isStart":false}),makeQuery(id+"F2.boolean.opBoolean","MERGE",FACE,{"derivedFrom":[makeQuery(id+"F1.opExtrude","SWEPT_FACE",FACE,{"disambiguationData":[OSD([subQ0])]}),makeQuery(id+"F2.opExtrude","SWEPT_FACE",FACE,{"disambiguationData":[OSD([subQ0])]})]})],"blendedInto":[makeQuery(id+"F2.boolean.opBoolean","MERGE",FACE,{"derivedFrom":[makeQuery(id+"F1.opExtrude","SWEPT_FACE",FACE,{"disambiguationData":[OSD([subQ0])]}),makeQuery(id+"F2.opExtrude","SWEPT_FACE",FACE,{"disambiguationData":[OSD([subQ0])]})]})]})])]});}
            fillet(context, id + "F11", {"entities" : qUnion([Q0, Q1, Q2]), "radius" : 1 * mm, "tangentPropagation" : true, "allowEdgeOverflow" : false});
        }
        {
            var Q0;
            {var subQ0=sQuery(id+"F0.wireOp",EDGE,"E0.bottom");Q0=makeQuery(id+"F9.boolean.opBoolean","SPLIT",EDGE,{"disambiguationData":[TD([makeQuery(id+"F9.opExtrude","SWEPT_FACE",FACE,{"disambiguationData":[OSD([sQuery(id+"F8.wireOp",EDGE,"E18.left")])]})])],"derivedFrom":makeQuery(id+"F7.opExtrude","CAP_EDGE",EDGE,{"disambiguationData":[OSD([subQ0])],"isStart":false})});}
            var Q1;
            {var subQ0=sQuery(id+"F0.wireOp",EDGE,"E0.bottom");Q1=makeQuery(id+"F10.opFillet","BLEND_EDGE",EDGE,{"blendedFrom":[makeQuery(id+"F9.boolean.opBoolean","COPY",EDGE,{"derivedFrom":makeQuery(id+"F9.opExtrude","CAP_EDGE",EDGE,{"disambiguationData":[OSD([sQuery(id+"F8.wireOp",EDGE,"E18.left")])],"isStart":true})}),makeQuery(id+"F7.boolean.opBoolean","MERGE",FACE,{"derivedFrom":[makeQuery(id+"F2.boolean.opBoolean","MERGE",FACE,{"derivedFrom":[makeQuery(id+"F1.opExtrude","SWEPT_FACE",FACE,{"disambiguationData":[OSD([subQ0])]}),makeQuery(id+"F2.opExtrude","SWEPT_FACE",FACE,{"disambiguationData":[OSD([subQ0])]})]}),makeQuery(id+"F7.opExtrude","SWEPT_FACE",FACE,{"disambiguationData":[OSD([subQ0])]})]})],"blendedInto":[makeQuery(id+"F7.boolean.opBoolean","MERGE",FACE,{"derivedFrom":[makeQuery(id+"F2.boolean.opBoolean","MERGE",FACE,{"derivedFrom":[makeQuery(id+"F1.opExtrude","SWEPT_FACE",FACE,{"disambiguationData":[OSD([subQ0])]}),makeQuery(id+"F2.opExtrude","SWEPT_FACE",FACE,{"disambiguationData":[OSD([subQ0])]})]}),makeQuery(id+"F7.opExtrude","SWEPT_FACE",FACE,{"disambiguationData":[OSD([subQ0])]})]})]});}
            var Q2;
            {var subQ0=sQuery(id+"F0.wireOp",EDGE,"E0.bottom");Q2=makeQuery(id+"F9.boolean.opBoolean","SPLIT",EDGE,{"disambiguationData":[TD([makeQuery(id+"F9.opExtrude","SWEPT_FACE",FACE,{"disambiguationData":[OSD([sQuery(id+"F8.wireOp",EDGE,"E18.right")])]})])],"derivedFrom":makeQuery(id+"F7.opExtrude","CAP_EDGE",EDGE,{"disambiguationData":[OSD([subQ0])],"isStart":false})});}
            var Q3;
            {var subQ0=sQuery(id+"F0.wireOp",EDGE,"E0.bottom");Q3=makeQuery(id+"F10.opFillet","BLEND_EDGE",EDGE,{"blendedFrom":[makeQuery(id+"F9.boolean.opBoolean","COPY",EDGE,{"derivedFrom":makeQuery(id+"F9.opExtrude","CAP_EDGE",EDGE,{"disambiguationData":[OSD([sQuery(id+"F8.wireOp",EDGE,"E18.right")])],"isStart":true})}),makeQuery(id+"F7.boolean.opBoolean","MERGE",FACE,{"derivedFrom":[makeQuery(id+"F2.boolean.opBoolean","MERGE",FACE,{"derivedFrom":[makeQuery(id+"F1.opExtrude","SWEPT_FACE",FACE,{"disambiguationData":[OSD([subQ0])]}),makeQuery(id+"F2.opExtrude","SWEPT_FACE",FACE,{"disambiguationData":[OSD([subQ0])]})]}),makeQuery(id+"F7.opExtrude","SWEPT_FACE",FACE,{"disambiguationData":[OSD([subQ0])]})]})],"blendedInto":[makeQuery(id+"F7.boolean.opBoolean","MERGE",FACE,{"derivedFrom":[makeQuery(id+"F2.boolean.opBoolean","MERGE",FACE,{"derivedFrom":[makeQuery(id+"F1.opExtrude","SWEPT_FACE",FACE,{"disambiguationData":[OSD([subQ0])]}),makeQuery(id+"F2.opExtrude","SWEPT_FACE",FACE,{"disambiguationData":[OSD([subQ0])]})]}),makeQuery(id+"F7.opExtrude","SWEPT_FACE",FACE,{"disambiguationData":[OSD([subQ0])]})]})]});}
            fillet(context, id + "F12", {"entities" : qUnion([Q0, Q1, Q2, Q3]), "radius" : 8 * mm, "tangentPropagation" : true, "allowEdgeOverflow" : false});
        }
        {
            var Q0;
            Q0=makeQuery(id+"F9.boolean.opBoolean","COPY",EDGE,{"derivedFrom":makeQuery(id+"F9.opExtrude","CAP_EDGE",EDGE,{"disambiguationData":[OSD([sQuery(id+"F8.wireOp",EDGE,"E18.top")])],"isStart":true})});
            var Q1;
            {var subQ0=sQuery(id+"F0.wireOp",EDGE,"E10.MirrorCS");var subQ1=sQuery(id+"F0.wireOp",EDGE,"E9");var subQ2=sQuery(id+"F0.wireOp",EDGE,"E4");var subQ3=sQuery(id+"F0.wireOp",EDGE,"E3.MirrorCS");var subQ4=sQuery(id+"F0.wireOp",EDGE,"E2");var subQ5=sQuery(id+"F0.wireOp",EDGE,"E0.bottom");Q1=makeQuery(id+"F9.boolean.opBoolean","INTERSECT",EDGE,{"derivedFrom":[makeQuery(id+"F2.boolean.opBoolean","MERGE",FACE,{"derivedFrom":[makeQuery(id+"F1.opExtrude","CAP_FACE",FACE,{"disambiguationData":[OSD([subQ5,subQ4,subQ3,subQ2,sQuery(id+"F0.wireOp",EDGE,"E5"),sQuery(id+"F0.wireOp",EDGE,"E6"),sQuery(id+"F0.wireOp",EDGE,"E7"),sQuery(id+"F0.wireOp",EDGE,"E8"),subQ1,subQ0,sQuery(id+"F0.wireOp",EDGE,"E17.bottom"),sQuery(id+"F0.wireOp",EDGE,"E17.top"),sQuery(id+"F0.wireOp",EDGE,"E17.left"),sQuery(id+"F0.wireOp",EDGE,"E17.right")])],"isStart":true}),makeQuery(id+"F2.opExtrude","CAP_FACE",FACE,{"disambiguationData":[OSD([subQ5,subQ4,subQ3,subQ2,subQ1,subQ0,sQuery(id+"F0.wireOp",EDGE,"E13"),sQuery(id+"F0.wireOp",EDGE,"E14"),sQuery(id+"F0.wireOp",EDGE,"E15"),sQuery(id+"F0.wireOp",EDGE,"E16")])],"isStart":true})]}),makeQuery(id+"F9.opExtrude","SWEPT_FACE",FACE,{"disambiguationData":[OSD([sQuery(id+"F8.wireOp",EDGE,"E18.top")])]})]});}
            fillet(context, id + "F13", {"entities" : qUnion([Q0, Q1]), "radius" : 2 * mm, "tangentPropagation" : true, "allowEdgeOverflow" : false});
        }
        {
            var Q0;
            Q0=qCreatedBy(makeId("Front.planeOp"),FACE);
            var sketch = newSketch(context, id + "F14", { "sketchPlane" : qUnion([Q0])});
            skCircle(sketch, "E19", {"center": v(-12.08, 7.29) * mm, "radius": 4.5 * mm});
            skSolve(sketch);
        }
        {
            var Q0;
            Q0=makeQuery(id+"F14.imprint","IMPRINT",FACE,{"disambiguationData":[TD([[makeQuery(id+"F14.imprint","IMPRINT",EDGE,{"derivedFrom":sQuery(id+"F14.wireOp",EDGE,"E19")}),1.0]])]});
            var Q1;
            Q1=sQuery(id+"F14.wireOp",EDGE,"E19");
            extrude(context, id + "F15", {"entities" : qUnion([Q0]), "operationType" : NewBodyOperationType.REMOVE, "surfaceEntities" : qUnion([Q1]), "depth" : 70 * mm});
        }
    });
